# Revit family: Ascoli Triple Round
name_source: partatom
category: Lighting Fixtures
revit_build: Autodesk Revit 2018 (Build: 20170927_1515(x64)
units: mm (PartAtom-declared; Revit-internal decimal feet)

## family parameters
Always vertical = Yes
Cut with Voids When Loaded = No
Host = Ceiling
Light Source = Yes
OmniClass Number = 23.80.70.11
OmniClass Title = Luminaries for Internal Lighting
Part Type = Normal
Room Calculation Point = No
Round Connector Dimension = Use Diameter
Shared = No

## types (2) — shared parameters
Color Filter = 16777215
Dimming Lamp Color Temperature Shift = <None>
Light Source Symbol Size = 600 mm

## per-type parameters (varying)
| type | Dimmable | Dimming Method | Driver Required | Efficacy (lm/w) | Electrical Class | Lamp | Light Source Fixed | Location Rating | Main Finish | Main Material | Power (Watts) | Product Code | Product Location | Product Name | Product SKU |
| CE | Lamp Dependant | Lamp Dependant | No | Lamp Dependant | 2 | GU10 | No | IP20 | Various | Mild Steel | 50W | Various | Indoor Ceiling or Wall | Ascoli Triple Round | Various |
| ETL |  |  |  |  |  |  |  |  |  |  |  |  |  |  |  |

## geometry (parser evidence)
native form markers: Sweep x2
no freeform markers — native parametric forms only
